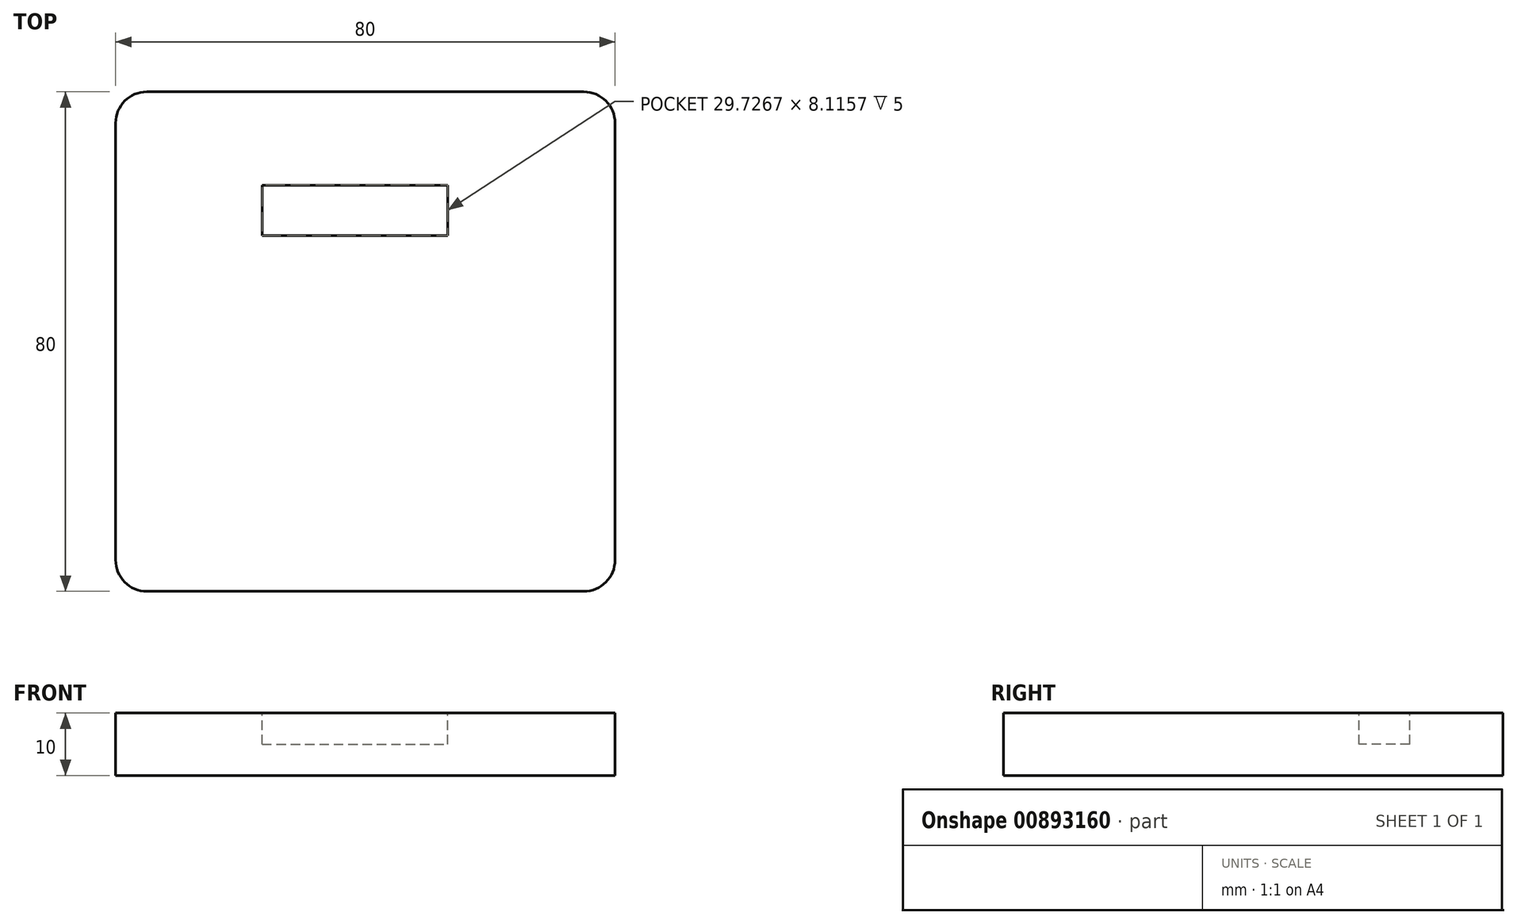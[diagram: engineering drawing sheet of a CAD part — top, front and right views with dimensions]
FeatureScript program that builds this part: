
annotation { "Feature Type Name" : "Feature", "Feature Type Description" : "" }
export const myFeature = defineFeature(function(context is Context, id is Id, definition is map)
    precondition{}
    {
        {
            var Q0;
            Q0=qCreatedBy(makeId("Top.planeOp"),FACE);
            var sketch = newSketch(context, id + "F0", { "sketchPlane" : qUnion([Q0])});
            skLineSegment(sketch, "E0.bottom", {"start": v(-69.27, 23.05) * mm, "end": v(10.73, 23.05) * mm});
            skLineSegment(sketch, "E0.top", {"start": v(-69.27, -56.95) * mm, "end": v(10.73, -56.95) * mm});
            skLineSegment(sketch, "E0.left", {"start": v(-69.27, 23.05) * mm, "end": v(-69.27, -56.95) * mm});
            skLineSegment(sketch, "E0.right", {"start": v(10.73, 23.05) * mm, "end": v(10.73, -56.95) * mm});
            skSolve(sketch);
        }
        {
            var Q0;
            Q0 = qSketchRegion(id + "F0", true);
            extrude(context, id + "F1", {"entities" : qUnion([Q0]), "depth" : 10 * mm, "offsetDistance" : 25 * mm});
        }
        {
            var Q0;
            Q0=makeQuery(id+"F1.opExtrude","SWEPT_EDGE",EDGE,{"disambiguationData":[OSD([sQuery(id+"F0.wireOp",EDGE,"E0.bottom"),sQuery(id+"F0.wireOp",EDGE,"E0.left")])]});
            var Q1;
            Q1=makeQuery(id+"F1.opExtrude","SWEPT_EDGE",EDGE,{"disambiguationData":[OSD([sQuery(id+"F0.wireOp",EDGE,"E0.top"),sQuery(id+"F0.wireOp",EDGE,"E0.left")])]});
            var Q2;
            Q2=makeQuery(id+"F1.opExtrude","SWEPT_EDGE",EDGE,{"disambiguationData":[OSD([sQuery(id+"F0.wireOp",EDGE,"E0.top"),sQuery(id+"F0.wireOp",EDGE,"E0.right")])]});
            var Q3;
            Q3=makeQuery(id+"F1.opExtrude","SWEPT_EDGE",EDGE,{"disambiguationData":[OSD([sQuery(id+"F0.wireOp",EDGE,"E0.bottom"),sQuery(id+"F0.wireOp",EDGE,"E0.right")])]});
            fillet(context, id + "F2", {"entities" : qUnion([Q0, Q1, Q2, Q3]), "radius" : 5 * mm, "tangentPropagation" : true, "allowEdgeOverflow" : false});
        }
        {
            var Q0;
            Q0=makeQuery(id+"F1.opExtrude","CAP_FACE",FACE,{"disambiguationData":[OSD([sQuery(id+"F0.wireOp",EDGE,"E0.bottom"),sQuery(id+"F0.wireOp",EDGE,"E0.top"),sQuery(id+"F0.wireOp",EDGE,"E0.left"),sQuery(id+"F0.wireOp",EDGE,"E0.right")])],"isStart":false});
            var sketch = newSketch(context, id + "F3", { "sketchPlane" : qUnion([Q0])});
            skLineSegment(sketch, "E1.bottom", {"start": v(-45.8, 8.12) * mm, "end": v(-16.08, 8.12) * mm});
            skLineSegment(sketch, "E1.top", {"start": v(-45.8, 0) * mm, "end": v(-16.08, 0) * mm});
            skLineSegment(sketch, "E1.left", {"start": v(-45.8, 8.12) * mm, "end": v(-45.8, 0) * mm});
            skLineSegment(sketch, "E1.right", {"start": v(-16.08, 8.12) * mm, "end": v(-16.08, 0) * mm});
            skSolve(sketch);
        }
        {
            var Q0;
            Q0 = qSketchRegion(id + "F3", true);
            extrude(context, id + "F4", {"entities" : qUnion([Q0]), "operationType" : NewBodyOperationType.REMOVE, "oppositeDirection" : true, "depth" : 5 * mm, "offsetDistance" : 25 * mm});
        }
    });
